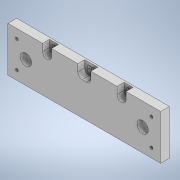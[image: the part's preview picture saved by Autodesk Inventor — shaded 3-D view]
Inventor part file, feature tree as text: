
AUTODESK INVENTOR PART (.ipt)
format: ipt  version: 2021 (Build 250183000, 183)  size: 255,488 bytes
history: native  units: in
note: dims shown in document units (in); Inventor stores cm internally (conversion verified against a paired STEP export)
features: sketch x6, extrude x3, hole x3, chamfer x3
ambient origin geometry x8: Origin, YZ Plane, XZ Plane, XY Plane, X Axis, Y Axis, Z Axis, Center Point
bodies: Solid1 (feature_tree)
feature tree (15):
  extrude  "Extrusion1"  Depth=0.9843in
  hole  "Hole1"  [1 undecoded]
  extrude  "Extrusion2"  Depth=2.5591in
  chamfer  "Chamfer1"  Distance=0.3937in
  hole  "Hole2"  [1 undecoded]
  extrude  "Extrusion3"  Depth=0.3937in
  chamfer  "Chamfer2"  Distance=3.3465in
  chamfer  "Chamfer3"  Distance=0.7874in
  hole  "Hole3"  [1 undecoded]
  sketch  "Sketch1"  dims[d0=3.3465in d1=0.9843in]
  sketch  "Sketch2"  dims[d2=0.25in d3=0.0in d4=0.9843in]
  sketch  "Sketch3"  dims[d5=0.4921in d6=2.5591in]
  sketch  "Sketch4"  dims[d7=0.3937in]
  sketch  "Sketch5"  dims[d8=3.3465in]
  sketch  "Sketch6"  dims[d9=0.25in d10=0.75in d11=0.375in d12=0.25in d13=0.5635in d14=1.0in d15=0.8108in d16=0.3937in d17=0.3937in d18=1.7717in d19=3.3465in d20=0.7874in d21=0.1969in d22=0.6693in d23=0.9843in d24=0.1575in d25=0.0787in d26=0.0787in d27=0.1181in d28=0.1181in d29=0.0591in d30=0.0in d31=0.0197in d32=0.0787in d33=45.0deg d34=0.4616in d35=0.3374in d36=1.2333in d37=1.3219in d38=2.0935in d39=0.4656in d40=0.0472in d41=0.2362in d42=0.1575in d43=0.0787in d44=90.0deg d45=0.315in d46=0.8108in d47=0.1969in d48=0.1969in d49=0.0984in d50=0.0984in d51=0.1516in d52=0.0in d53=0.0197in d54=0.0787in d55=45.0deg d56=0.0591in d57=0.0197in d58=0.0787in d59=45.0deg d60=0.1969in d61=0.1969in d62=0.1969in d63=0.1969in d64=0.0617in d65=0.1575in d66=0.1575in d67=0.0787in d68=90.0deg d69=0.248in d70=0.8108in]
note: 3 required parameter values undecoded (feature->parameter linkage not recoverable at this tier; creation-order binding heuristic only, values carry confidence <= 0.55)
